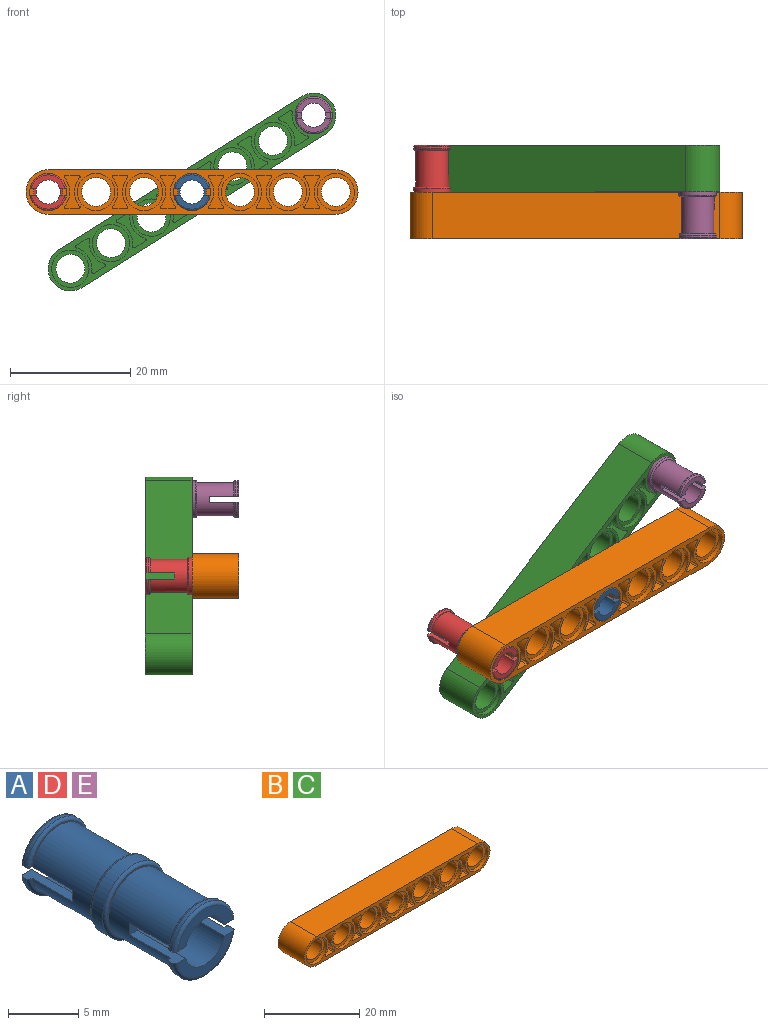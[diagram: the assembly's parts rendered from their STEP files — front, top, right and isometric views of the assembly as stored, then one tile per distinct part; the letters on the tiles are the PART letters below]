
ASSEMBLY  parts=5 mates=4
PART A: 40 faces, bbox 6.7x15.5x6.7 mm
  f0: cylinder r=3.1mm len=6.12mm, axis (0,1,0), area 2.6mm2, adj f11,f14,f16,f17
  f1: plane 5.61x2.35mm, normal (0,-1,0), area 5.6mm2, adj f2,f11,f14,f16
  f2: cylinder r=2mm len=15.52mm, axis (0,1,0), area 175.3mm2, adj f1,f6,f10,f11,f12,f13,f14,f15
  f3: cylinder r=2.75mm len=6.16mm, axis (0,1,0), area 98.2mm2, adj f4,f8,f9,f10,f11,f12,f13,f14
  f4: plane 5.61x2.35mm, normal (0,1,0), area 0.8mm2, adj f3,f11,f14,f17
  f5: cylinder r=3.1mm len=6.12mm, axis (0,1,0), area 2.6mm2, adj f10,f15,f18,f20
  f6: plane 5.61x2.35mm, normal (0,-1,0), area 5.6mm2, adj f2,f10,f15,f18
  f7: cylinder r=3.1mm len=6.2mm, axis (0,1,0), area 21.4mm2, adj f19,f38
  f8: plane 5.7x5.7mm, normal (0,-1,0), area 1.8mm2, adj f3,f19
  f9: plane 5.61x2.35mm, normal (0,1,0), area 0.8mm2, adj f3,f10,f15,f20
  f10: plane 4.9x1.14mm, normal (0,0,1), area 4mm2, adj f2,f3,f5,f6,f9,f12,f18,f20
  f11: plane 4.9x1.14mm, normal (0,0,-1), area 4mm2, adj f0,f1,f2,f3,f4,f12,f16,f17
  f12: plane 1x0.81mm, normal (0,-1,0), area 0.8mm2, adj f2,f3,f10,f11
  f13: plane 1x0.81mm, normal (0,-1,0), area 0.8mm2, adj f2,f3,f14,f15
  f14: plane 4.9x1.14mm, normal (0,0,-1), area 4mm2, adj f0,f1,f2,f3,f4,f13,f16,f17
  f15: plane 4.9x1.14mm, normal (0,0,1), area 4mm2, adj f2,f3,f5,f6,f9,f13,f18,f20
  f16: torus R=2.85mm, axis (0,1,0), area 3.3mm2, adj f0,f1,f11,f14
  f17: torus R=2.85mm, axis (0,-1,0), area 3.3mm2, adj f0,f4,f11,f14
  f18: torus R=2.85mm, axis (0,1,0), area 3.3mm2, adj f5,f6,f10,f15
  f19: torus R=2.85mm, axis (0,1,0), area 7.4mm2, adj f7,f8
  f20: torus R=2.85mm, axis (0,-1,0), area 3.3mm2, adj f5,f9,f10,f15
  f21: cylinder r=3.1mm len=6.12mm, axis (0,-1,0), area 2.6mm2, adj f30,f33,f35,f36
  f22: plane 5.61x2.35mm, normal (0,1,0), area 5.6mm2, adj f2,f30,f33,f35
  f23: cylinder r=2.75mm len=6.16mm, axis (0,-1,0), area 98.2mm2, adj f24,f27,f28,f29,f30,f31,f32,f33
  f24: plane 5.61x2.35mm, normal (0,-1,0), area 0.8mm2, adj f23,f30,f33,f36
  f25: cylinder r=3.1mm len=6.12mm, axis (0,-1,0), area 2.6mm2, adj f29,f34,f37,f39
  f26: plane 5.61x2.35mm, normal (0,1,0), area 5.6mm2, adj f2,f29,f34,f37
  f27: plane 5.7x5.7mm, normal (0,1,0), area 1.8mm2, adj f23,f38
  f28: plane 5.61x2.35mm, normal (0,-1,0), area 0.8mm2, adj f23,f29,f34,f39
  f29: plane 4.9x1.14mm, normal (0,0,1), area 4mm2, adj f2,f23,f25,f26,f28,f31,f37,f39
  f30: plane 4.9x1.14mm, normal (0,0,-1), area 4mm2, adj f2,f21,f22,f23,f24,f31,f35,f36
  f31: plane 1x0.81mm, normal (0,1,0), area 0.8mm2, adj f2,f23,f29,f30
  f32: plane 1x0.81mm, normal (0,1,0), area 0.8mm2, adj f2,f23,f33,f34
  f33: plane 4.9x1.14mm, normal (0,0,-1), area 4mm2, adj f2,f21,f22,f23,f24,f32,f35,f36
  f34: plane 4.9x1.14mm, normal (0,0,1), area 4mm2, adj f2,f23,f25,f26,f28,f32,f37,f39
  f35: torus R=2.85mm, axis (0,-1,0), area 3.3mm2, adj f21,f22,f30,f33
  f36: torus R=2.85mm, axis (0,1,0), area 3.3mm2, adj f21,f24,f30,f33
  f37: torus R=2.85mm, axis (0,-1,0), area 3.3mm2, adj f25,f26,f29,f34
  f38: torus R=2.85mm, axis (0,-1,0), area 7.4mm2, adj f7,f27
  f39: torus R=2.85mm, axis (0,1,0), area 3.3mm2, adj f25,f28,f29,f34
PART B: 149 faces, bbox 55.2x7.8x7.4 mm
  f0: plane 55.2x7.38mm, normal (0,-1,0), area 134.9mm2, adj f1,f2,f3,f4,f5,f6,f7,f8
  f1: cylinder r=3.69mm len=7.76mm, axis (0,1,0), area 90mm2, adj f0,f2,f9,f80
  f2: plane 47.82x7.76mm, normal (0,0,-1), area 371.1mm2, adj f0,f1,f3,f80
  f3: cylinder r=3.69mm len=7.76mm, axis (0,1,0), area 90mm2, adj f0,f2,f9,f80
  f4: cylinder r=3.1mm len=6.2mm, axis (0,1,0), area 15.6mm2, adj f0,f17
  f5: cylinder r=3.1mm len=6.2mm, axis (0,1,0), area 15.6mm2, adj f0,f19
  f6: cylinder r=3.1mm len=6.2mm, axis (0,1,0), area 15.6mm2, adj f0,f21
  f7: cylinder r=3.1mm len=6.2mm, axis (0,1,0), area 15.6mm2, adj f0,f23
  f8: cylinder r=3.1mm len=6.2mm, axis (0,1,0), area 15.6mm2, adj f0,f25
  f9: plane 47.82x7.76mm, normal (0,0,1), area 371.1mm2, adj f0,f1,f3,f80
  f10: cylinder r=3.1mm len=6.2mm, axis (0,1,0), area 15.6mm2, adj f0,f13
  f11: cylinder r=3.1mm len=6.2mm, axis (0,1,0), area 15.6mm2, adj f0,f15
  f12: cylinder r=2.4mm len=6.16mm, axis (0,1,0), area 92.9mm2, adj f13,f88
  f13: plane 6.2x6.2mm, normal (0,-1,0), area 12.1mm2, adj f10,f12
  f14: cylinder r=2.4mm len=6.16mm, axis (0,1,0), area 92.9mm2, adj f15,f89
  f15: plane 6.2x6.2mm, normal (0,-1,0), area 12.1mm2, adj f11,f14
  f16: cylinder r=2.4mm len=6.16mm, axis (0,1,0), area 92.9mm2, adj f17,f90
  f17: plane 6.2x6.2mm, normal (0,-1,0), area 12.1mm2, adj f4,f16
  f18: cylinder r=2.4mm len=6.16mm, axis (0,1,0), area 92.9mm2, adj f19,f91
  f19: plane 6.2x6.2mm, normal (0,-1,0), area 12.1mm2, adj f5,f18
  f20: cylinder r=2.4mm len=6.16mm, axis (0,1,0), area 92.9mm2, adj f21,f92
  f21: plane 6.2x6.2mm, normal (0,-1,0), area 12.1mm2, adj f6,f20
  f22: cylinder r=2.4mm len=6.16mm, axis (0,1,0), area 92.9mm2, adj f23,f93
  f23: plane 6.2x6.2mm, normal (0,-1,0), area 12.1mm2, adj f7,f22
  f24: cylinder r=2.4mm len=6.16mm, axis (0,1,0), area 92.9mm2, adj f25,f94
  f25: plane 6.2x6.2mm, normal (0,-1,0), area 12.1mm2, adj f8,f24
  f26: plane 3.5x2.11mm, normal (0,0,-1), area 7.4mm2, adj f0,f30,f56,f59
  f27: cylinder r=3.6mm len=4.68mm, axis (0,-1,0), area 17.8mm2, adj f0,f30,f58,f59
  f28: plane 3.5x2.11mm, normal (0,0,1), area 7.4mm2, adj f0,f30,f57,f58
  f29: cylinder r=3.6mm len=4.68mm, axis (0,-1,0), area 17.8mm2, adj f0,f30,f56,f57
  f30: plane 5.5x2.61mm, normal (0,-1,0), area 8.2mm2, adj f26,f27,f28,f29,f56,f57,f58,f59
  f31: plane 3.5x2.11mm, normal (0,0,-1), area 7.4mm2, adj f0,f35,f60,f63
  f32: cylinder r=3.6mm len=4.68mm, axis (0,-1,0), area 17.8mm2, adj f0,f35,f62,f63
  f33: plane 3.5x2.11mm, normal (0,0,1), area 7.4mm2, adj f0,f35,f61,f62
  f34: cylinder r=3.6mm len=4.68mm, axis (0,-1,0), area 17.8mm2, adj f0,f35,f60,f61
  f35: plane 5.5x2.61mm, normal (0,-1,0), area 8.2mm2, adj f31,f32,f33,f34,f60,f61,f62,f63
  f36: plane 3.5x2.11mm, normal (0,0,-1), area 7.4mm2, adj f0,f40,f64,f67
  f37: cylinder r=3.6mm len=4.68mm, axis (0,-1,0), area 17.8mm2, adj f0,f40,f66,f67
  f38: plane 3.5x2.11mm, normal (0,0,1), area 7.4mm2, adj f0,f40,f65,f66
  f39: cylinder r=3.6mm len=4.68mm, axis (0,-1,0), area 17.8mm2, adj f0,f40,f64,f65
  f40: plane 5.5x2.61mm, normal (0,-1,0), area 8.2mm2, adj f36,f37,f38,f39,f64,f65,f66,f67
  f41: plane 3.5x2.11mm, normal (0,0,-1), area 7.4mm2, adj f0,f45,f68,f71
  f42: cylinder r=3.6mm len=4.68mm, axis (0,-1,0), area 17.8mm2, adj f0,f45,f70,f71
  f43: plane 3.5x2.11mm, normal (0,0,1), area 7.4mm2, adj f0,f45,f69,f70
  f44: cylinder r=3.6mm len=4.68mm, axis (0,-1,0), area 17.8mm2, adj f0,f45,f68,f69
  f45: plane 5.5x2.61mm, normal (0,-1,0), area 8.2mm2, adj f41,f42,f43,f44,f68,f69,f70,f71
  f46: plane 3.5x2.11mm, normal (0,0,-1), area 7.4mm2, adj f0,f50,f72,f75
  f47: cylinder r=3.6mm len=4.68mm, axis (0,-1,0), area 17.8mm2, adj f0,f50,f72,f73
  f48: plane 3.5x2.11mm, normal (0,0,1), area 7.4mm2, adj f0,f50,f73,f74
  f49: cylinder r=3.6mm len=4.68mm, axis (0,-1,0), area 17.8mm2, adj f0,f50,f74,f75
  f50: plane 5.5x2.61mm, normal (0,-1,0), area 8.2mm2, adj f46,f47,f48,f49,f72,f73,f74,f75
  f51: plane 3.5x2.11mm, normal (0,0,-1), area 7.4mm2, adj f0,f55,f76,f79
  f52: cylinder r=3.6mm len=4.68mm, axis (0,-1,0), area 17.8mm2, adj f0,f55,f78,f79
  f53: plane 3.5x2.11mm, normal (0,0,1), area 7.4mm2, adj f0,f55,f77,f78
  f54: cylinder r=3.6mm len=4.68mm, axis (0,-1,0), area 17.8mm2, adj f0,f55,f76,f77
  f55: plane 5.5x2.61mm, normal (0,-1,0), area 8.2mm2, adj f51,f52,f53,f54,f76,f77,f78,f79
  f56: cylinder r=0.25mm len=3.5mm, axis (0,-1,0), area 2mm2, adj f0,f26,f29,f30
  f57: cylinder r=0.25mm len=3.5mm, axis (0,-1,0), area 2mm2, adj f0,f28,f29,f30
  f58: cylinder r=0.25mm len=3.5mm, axis (0,-1,0), area 2mm2, adj f0,f27,f28,f30
  f59: cylinder r=0.25mm len=3.5mm, axis (0,-1,0), area 2mm2, adj f0,f26,f27,f30
  f60: cylinder r=0.25mm len=3.5mm, axis (0,-1,0), area 2mm2, adj f0,f31,f34,f35
  f61: cylinder r=0.25mm len=3.5mm, axis (0,-1,0), area 2mm2, adj f0,f33,f34,f35
  f62: cylinder r=0.25mm len=3.5mm, axis (0,-1,0), area 2mm2, adj f0,f32,f33,f35
  f63: cylinder r=0.25mm len=3.5mm, axis (0,-1,0), area 2mm2, adj f0,f31,f32,f35
  f64: cylinder r=0.25mm len=3.5mm, axis (0,-1,0), area 2mm2, adj f0,f36,f39,f40
  f65: cylinder r=0.25mm len=3.5mm, axis (0,-1,0), area 2mm2, adj f0,f38,f39,f40
  f66: cylinder r=0.25mm len=3.5mm, axis (0,-1,0), area 2mm2, adj f0,f37,f38,f40
  f67: cylinder r=0.25mm len=3.5mm, axis (0,-1,0), area 2mm2, adj f0,f36,f37,f40
  f68: cylinder r=0.25mm len=3.5mm, axis (0,-1,0), area 2mm2, adj f0,f41,f44,f45
  f69: cylinder r=0.25mm len=3.5mm, axis (0,-1,0), area 2mm2, adj f0,f43,f44,f45
  f70: cylinder r=0.25mm len=3.5mm, axis (0,-1,0), area 2mm2, adj f0,f42,f43,f45
  f71: cylinder r=0.25mm len=3.5mm, axis (0,-1,0), area 2mm2, adj f0,f41,f42,f45
  f72: cylinder r=0.25mm len=3.5mm, axis (0,-1,0), area 2mm2, adj f0,f46,f47,f50
  f73: cylinder r=0.25mm len=3.5mm, axis (0,-1,0), area 2mm2, adj f0,f47,f48,f50
  f74: cylinder r=0.25mm len=3.5mm, axis (0,-1,0), area 2mm2, adj f0,f48,f49,f50
  f75: cylinder r=0.25mm len=3.5mm, axis (0,-1,0), area 2mm2, adj f0,f46,f49,f50
  f76: cylinder r=0.25mm len=3.5mm, axis (0,-1,0), area 2mm2, adj f0,f51,f54,f55
  f77: cylinder r=0.25mm len=3.5mm, axis (0,-1,0), area 2mm2, adj f0,f53,f54,f55
  f78: cylinder r=0.25mm len=3.5mm, axis (0,-1,0), area 2mm2, adj f0,f52,f53,f55
  f79: cylinder r=0.25mm len=3.5mm, axis (0,-1,0), area 2mm2, adj f0,f51,f52,f55
  f80: plane 55.2x7.38mm, normal (0,1,0), area 134.9mm2, adj f1,f2,f3,f9,f81,f82,f83,f84
  f81: cylinder r=3.1mm len=6.2mm, axis (0,-1,0), area 15.6mm2, adj f80,f90
  f82: cylinder r=3.1mm len=6.2mm, axis (0,-1,0), area 15.6mm2, adj f80,f91
  f83: cylinder r=3.1mm len=6.2mm, axis (0,-1,0), area 15.6mm2, adj f80,f92
  f84: cylinder r=3.1mm len=6.2mm, axis (0,-1,0), area 15.6mm2, adj f80,f93
  f85: cylinder r=3.1mm len=6.2mm, axis (0,-1,0), area 15.6mm2, adj f80,f94
  f86: cylinder r=3.1mm len=6.2mm, axis (0,-1,0), area 15.6mm2, adj f80,f88
  f87: cylinder r=3.1mm len=6.2mm, axis (0,-1,0), area 15.6mm2, adj f80,f89
  f88: plane 6.2x6.2mm, normal (0,1,0), area 12.1mm2, adj f12,f86
  f89: plane 6.2x6.2mm, normal (0,1,0), area 12.1mm2, adj f14,f87
  f90: plane 6.2x6.2mm, normal (0,1,0), area 12.1mm2, adj f16,f81
  f91: plane 6.2x6.2mm, normal (0,1,0), area 12.1mm2, adj f18,f82
  f92: plane 6.2x6.2mm, normal (0,1,0), area 12.1mm2, adj f20,f83
  f93: plane 6.2x6.2mm, normal (0,1,0), area 12.1mm2, adj f22,f84
  f94: plane 6.2x6.2mm, normal (0,1,0), area 12.1mm2, adj f24,f85
  f95: plane 3.5x2.11mm, normal (0,0,-1), area 7.4mm2, adj f80,f99,f125,f128
  f96: cylinder r=3.6mm len=4.68mm, axis (0,1,0), area 17.8mm2, adj f80,f99,f127,f128
  f97: plane 3.5x2.11mm, normal (0,0,1), area 7.4mm2, adj f80,f99,f126,f127
  f98: cylinder r=3.6mm len=4.68mm, axis (0,1,0), area 17.8mm2, adj f80,f99,f125,f126
  f99: plane 5.5x2.61mm, normal (0,1,0), area 8.2mm2, adj f95,f96,f97,f98,f125,f126,f127,f128
  f100: plane 3.5x2.11mm, normal (0,0,-1), area 7.4mm2, adj f80,f104,f129,f132
  f101: cylinder r=3.6mm len=4.68mm, axis (0,1,0), area 17.8mm2, adj f80,f104,f131,f132
  f102: plane 3.5x2.11mm, normal (0,0,1), area 7.4mm2, adj f80,f104,f130,f131
  f103: cylinder r=3.6mm len=4.68mm, axis (0,1,0), area 17.8mm2, adj f80,f104,f129,f130
  f104: plane 5.5x2.61mm, normal (0,1,0), area 8.2mm2, adj f100,f101,f102,f103,f129,f130,f131,f132
  f105: plane 3.5x2.11mm, normal (0,0,-1), area 7.4mm2, adj f80,f109,f133,f136
  f106: cylinder r=3.6mm len=4.68mm, axis (0,1,0), area 17.8mm2, adj f80,f109,f135,f136
  f107: plane 3.5x2.11mm, normal (0,0,1), area 7.4mm2, adj f80,f109,f134,f135
  f108: cylinder r=3.6mm len=4.68mm, axis (0,1,0), area 17.8mm2, adj f80,f109,f133,f134
  f109: plane 5.5x2.61mm, normal (0,1,0), area 8.2mm2, adj f105,f106,f107,f108,f133,f134,f135,f136
  f110: plane 3.5x2.11mm, normal (0,0,-1), area 7.4mm2, adj f80,f114,f137,f140
  f111: cylinder r=3.6mm len=4.68mm, axis (0,1,0), area 17.8mm2, adj f80,f114,f139,f140
  f112: plane 3.5x2.11mm, normal (0,0,1), area 7.4mm2, adj f80,f114,f138,f139
  f113: cylinder r=3.6mm len=4.68mm, axis (0,1,0), area 17.8mm2, adj f80,f114,f137,f138
  f114: plane 5.5x2.61mm, normal (0,1,0), area 8.2mm2, adj f110,f111,f112,f113,f137,f138,f139,f140
  f115: plane 3.5x2.11mm, normal (0,0,-1), area 7.4mm2, adj f80,f119,f141,f144
  f116: cylinder r=3.6mm len=4.68mm, axis (0,1,0), area 17.8mm2, adj f80,f119,f141,f142
  f117: plane 3.5x2.11mm, normal (0,0,1), area 7.4mm2, adj f80,f119,f142,f143
  f118: cylinder r=3.6mm len=4.68mm, axis (0,1,0), area 17.8mm2, adj f80,f119,f143,f144
  f119: plane 5.5x2.61mm, normal (0,1,0), area 8.2mm2, adj f115,f116,f117,f118,f141,f142,f143,f144
  f120: plane 3.5x2.11mm, normal (0,0,-1), area 7.4mm2, adj f80,f124,f145,f148
  f121: cylinder r=3.6mm len=4.68mm, axis (0,1,0), area 17.8mm2, adj f80,f124,f147,f148
  f122: plane 3.5x2.11mm, normal (0,0,1), area 7.4mm2, adj f80,f124,f146,f147
  f123: cylinder r=3.6mm len=4.68mm, axis (0,1,0), area 17.8mm2, adj f80,f124,f145,f146
  f124: plane 5.5x2.61mm, normal (0,1,0), area 8.2mm2, adj f120,f121,f122,f123,f145,f146,f147,f148
  f125: cylinder r=0.25mm len=3.5mm, axis (0,1,0), area 2mm2, adj f80,f95,f98,f99
  f126: cylinder r=0.25mm len=3.5mm, axis (0,1,0), area 2mm2, adj f80,f97,f98,f99
  f127: cylinder r=0.25mm len=3.5mm, axis (0,1,0), area 2mm2, adj f80,f96,f97,f99
  f128: cylinder r=0.25mm len=3.5mm, axis (0,1,0), area 2mm2, adj f80,f95,f96,f99
  f129: cylinder r=0.25mm len=3.5mm, axis (0,1,0), area 2mm2, adj f80,f100,f103,f104
  f130: cylinder r=0.25mm len=3.5mm, axis (0,1,0), area 2mm2, adj f80,f102,f103,f104
  f131: cylinder r=0.25mm len=3.5mm, axis (0,1,0), area 2mm2, adj f80,f101,f102,f104
  f132: cylinder r=0.25mm len=3.5mm, axis (0,1,0), area 2mm2, adj f80,f100,f101,f104
  f133: cylinder r=0.25mm len=3.5mm, axis (0,1,0), area 2mm2, adj f80,f105,f108,f109
  f134: cylinder r=0.25mm len=3.5mm, axis (0,1,0), area 2mm2, adj f80,f107,f108,f109
  f135: cylinder r=0.25mm len=3.5mm, axis (0,1,0), area 2mm2, adj f80,f106,f107,f109
  f136: cylinder r=0.25mm len=3.5mm, axis (0,1,0), area 2mm2, adj f80,f105,f106,f109
  f137: cylinder r=0.25mm len=3.5mm, axis (0,1,0), area 2mm2, adj f80,f110,f113,f114
  f138: cylinder r=0.25mm len=3.5mm, axis (0,1,0), area 2mm2, adj f80,f112,f113,f114
  f139: cylinder r=0.25mm len=3.5mm, axis (0,1,0), area 2mm2, adj f80,f111,f112,f114
  f140: cylinder r=0.25mm len=3.5mm, axis (0,1,0), area 2mm2, adj f80,f110,f111,f114
  f141: cylinder r=0.25mm len=3.5mm, axis (0,1,0), area 2mm2, adj f80,f115,f116,f119
  f142: cylinder r=0.25mm len=3.5mm, axis (0,1,0), area 2mm2, adj f80,f116,f117,f119
  f143: cylinder r=0.25mm len=3.5mm, axis (0,1,0), area 2mm2, adj f80,f117,f118,f119
  f144: cylinder r=0.25mm len=3.5mm, axis (0,1,0), area 2mm2, adj f80,f115,f118,f119
  f145: cylinder r=0.25mm len=3.5mm, axis (0,1,0), area 2mm2, adj f80,f120,f123,f124
  f146: cylinder r=0.25mm len=3.5mm, axis (0,1,0), area 2mm2, adj f80,f122,f123,f124
  f147: cylinder r=0.25mm len=3.5mm, axis (0,1,0), area 2mm2, adj f80,f121,f122,f124
  f148: cylinder r=0.25mm len=3.5mm, axis (0,1,0), area 2mm2, adj f80,f120,f121,f124
PART C: same geometry as B
PART D: same geometry as A
PART E: same geometry as A
PLACE A rot(axis=(1,0,0),180deg) t=(29.73,7.76,7.72)mm
PLACE B t=(5.82,0,7.72)mm
PLACE C rot(axis=(0,-1,0),32.3deg) t=(9.51,7.76,-5.04)mm
PLACE D rot(axis=(1,0,0),180deg) t=(5.82,7.76,7.72)mm
PLACE E rot(axis=(0.03,1,-0.03),0deg) t=(49.95,0,20.49)mm
MATE revolute D.f0 <-> B.f12  axis (0,1,0) through (5.82,0,7.72)mm
MATE revolute E.f0 <-> C.f3  axis (0,-1,0) through (49.95,7.76,20.49)mm
MATE revolute A.f0 <-> B.f5  axis (0,1,0) through (29.73,0,7.72)mm
MATE revolute A.f0 <-> C.f5  axis (0,-1,0) through (29.73,7.76,7.72)mm
